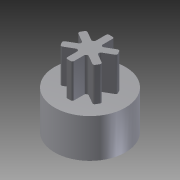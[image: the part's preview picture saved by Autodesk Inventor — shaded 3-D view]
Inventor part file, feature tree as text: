
AUTODESK INVENTOR PART (.ipt)
format: ipt  version: 2012 (Build 160160000, 160)  size: 200,192 bytes
history: native  units: mm
features: extrude x4, sketch x4, other x3, projected_geometry x2, fillet x1
ambient origin geometry x8: Origin, YZ Plane, XZ Plane, XY Plane, X Axis, Y Axis, Z Axis, Center Point
bodies: Solid1 (feature_tree)
feature tree (14):
  other  "ServoToScrewKey.ipt"
  extrude  "Extrusion1"  TaperAngle=0.0deg  [1 undecoded]
  extrude  "Extrusion2"  Depth=20.78461mm
  extrude  "Extrusion3"  Depth=10.0mm TaperAngle=0.0deg
  extrude  "Extrusion5"  Depth=1.0mm
  fillet  "Fillet1"  Radius=4.0mm
  other  "Solid2::ServoToScrewKey.ipt"
  other  "TaggingFeature1"
  sketch  "Sketch2"  dims[d0=10.0mm d1=0.0mm d2=0.0mm]
  projected_geometry  "Projected Loop1"
  sketch  "Sketch3"  dims[d3=12.0mm d4=0.0mm d5=20.78461mm]
  sketch  "Sketch4"  dims[d6=5.196152mm d7=10.0mm d8=0.0mm]
  projected_geometry  "Projected Loop2"
  sketch  "Sketch6"  dims[d20=1.0mm d21=1.0mm d22=4.0mm d23=60.0mm d25=360.0deg d27=10.0mm d28=0.0mm d29=0.5mm]
note: 1 required parameter value undecoded (feature->parameter linkage not recoverable at this tier; creation-order binding heuristic only, values carry confidence <= 0.55)
